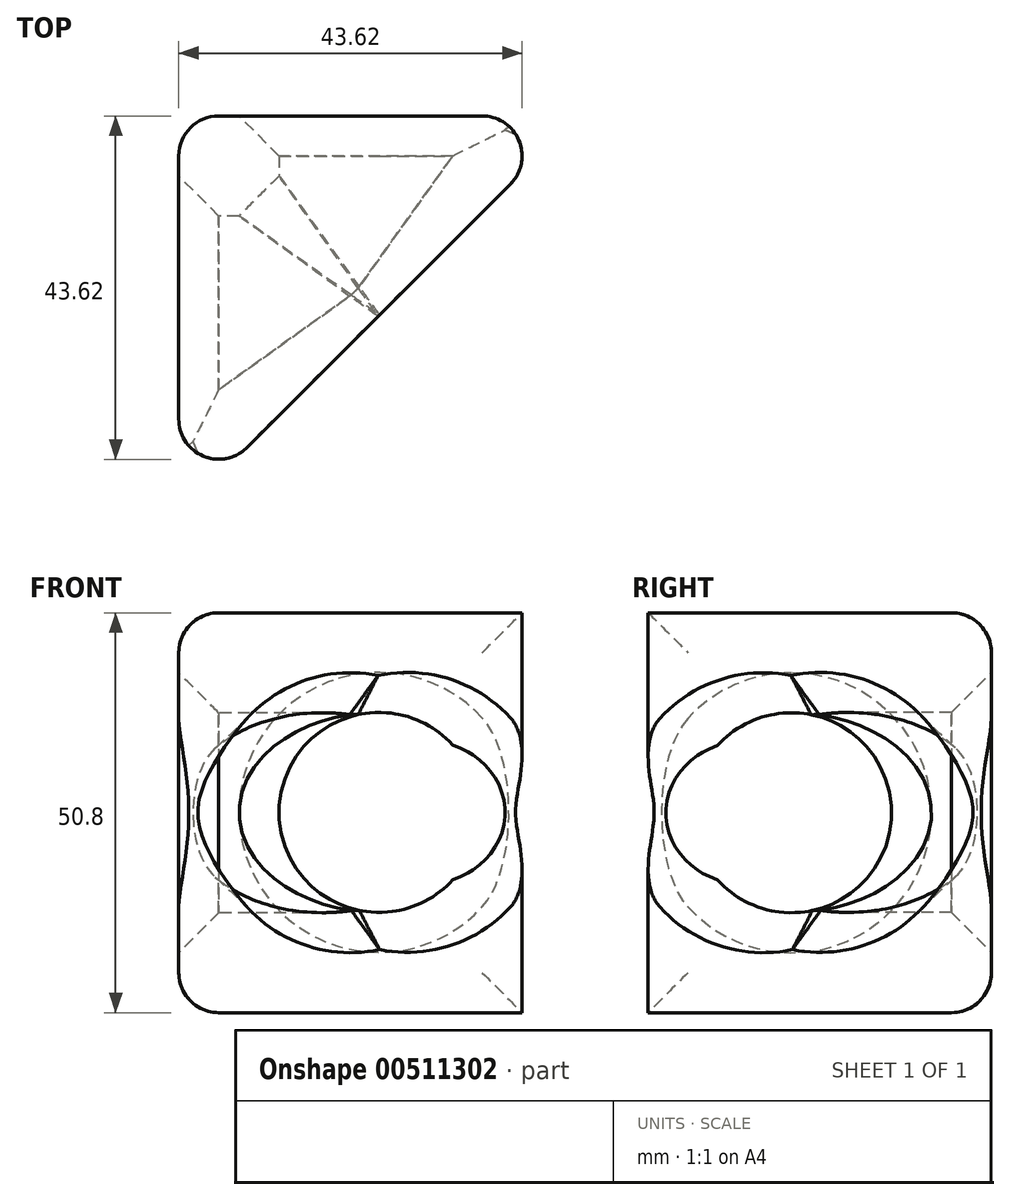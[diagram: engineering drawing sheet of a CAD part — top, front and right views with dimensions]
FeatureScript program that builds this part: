
annotation { "Feature Type Name" : "Feature", "Feature Type Description" : "" }
export const myFeature = defineFeature(function(context is Context, id is Id, definition is map)
    precondition{}
    {
        {
            var Q0;
            Q0=qCreatedBy(makeId("Front.planeOp"),FACE);
            var sketch = newSketch(context, id + "F0", { "sketchPlane" : qUnion([Q0])});
            skLineSegment(sketch, "E0", {"start": v(0, 0) * mm, "end": v(50.8, 0) * mm});
            skLineSegment(sketch, "E1", {"start": v(50.8, 0) * mm, "end": v(50.8, 50.8) * mm});
            skLineSegment(sketch, "E2", {"start": v(50.8, 50.8) * mm, "end": v(0, 50.8) * mm});
            skLineSegment(sketch, "E3", {"start": v(0, 0) * mm, "end": v(0, 50.8) * mm});
            skSolve(sketch);
        }
        {
            var Q0;
            Q0 = qSketchRegion(id + "F0", true);
            extrude(context, id + "F1", {"entities" : qUnion([Q0]), "depth" : 50.8 * mm, "offsetDistance" : 25.4 * mm});
        }
        {
            var Q0;
            Q0=makeQuery(id+"F1.opExtrude","CAP_FACE",FACE,{"disambiguationData":[OSD([sQuery(id+"F0.wireOp",EDGE,"E0"),sQuery(id+"F0.wireOp",EDGE,"E1"),sQuery(id+"F0.wireOp",EDGE,"E2"),sQuery(id+"F0.wireOp",EDGE,"E3")])],"isStart":false});
            var sketch = newSketch(context, id + "F2", { "sketchPlane" : qUnion([Q0])});
            skLineSegment(sketch, "E4", {"start": v(50.8, 50.8) * mm, "end": v(0, 0) * mm});
            skLineSegment(sketch, "E5", {"start": v(50.88, 0) * mm, "end": v(0, 50.88) * mm});
            skCircle(sketch, "E6", {"center": v(25.44, 25.44) * mm, "radius": 12.7 * mm});
            skSolve(sketch);
        }
        {
            var Q0;
            Q0 = qSketchRegion(id + "F2", true);
            extrude(context, id + "F3", {"entities" : qUnion([Q0]), "operationType" : NewBodyOperationType.REMOVE, "oppositeDirection" : true, "depth" : 50.8 * mm, "offsetDistance" : 25.4 * mm});
        }
        {
            var Q0;
            Q0=makeQuery(id+"F1.opExtrude","SWEPT_FACE",FACE,{"disambiguationData":[OSD([sQuery(id+"F0.wireOp",EDGE,"E3")])]});
            var sketch = newSketch(context, id + "F4", { "sketchPlane" : qUnion([Q0])});
            skLineSegment(sketch, "E7", {"start": v(50.8, 50.8) * mm, "end": v(0, 0) * mm});
            skLineSegment(sketch, "E8", {"start": v(50.8, 0) * mm, "end": v(0, 50.8) * mm});
            skCircle(sketch, "E9", {"center": v(25.4, 25.4) * mm, "radius": 12.7 * mm});
            skSolve(sketch);
        }
        {
            var Q0;
            Q0 = qSketchRegion(id + "F4", true);
            extrude(context, id + "F5", {"entities" : qUnion([Q0]), "operationType" : NewBodyOperationType.REMOVE, "oppositeDirection" : true, "depth" : 50.8 * mm, "offsetDistance" : 25.4 * mm});
        }
        {
            var Q0;
            Q0=makeQuery(id+"F1.opExtrude","SWEPT_FACE",FACE,{"disambiguationData":[OSD([sQuery(id+"F0.wireOp",EDGE,"E0")])]});
            var sketch = newSketch(context, id + "F6", { "sketchPlane" : qUnion([Q0])});
            skLineSegment(sketch, "E10", {"start": v(0, 0) * mm, "end": v(50.8, 50.8) * mm});
            skLineSegment(sketch, "E11", {"start": v(50.8, 50.8) * mm, "end": v(50.8, 0) * mm});
            skLineSegment(sketch, "E12", {"start": v(50.8, 0) * mm, "end": v(0, 50.8) * mm});
            skCircle(sketch, "E13", {"center": v(25.4, 25.4) * mm, "radius": 12.7 * mm});
            skSolve(sketch);
        }
        {
            var Q0;
            {var subQ0=sQuery(id+"F6.wireOp",EDGE,"E13");var subQ1=sQuery(id+"F6.wireOp",EDGE,"E10");var subQ2=makeQuery(id+"F6.imprint","INTERSECT",VERTEX,{"disambiguationData":[OD(0.0)],"derivedFrom":[subQ1,subQ0]});Q0=makeQuery(id+"F6.imprint","IMPRINT",FACE,{"disambiguationData":[TD([[makeQuery(id+"F6.imprint","IMPRINT",EDGE,{"disambiguationData":[TD([[subQ2,-1.0]])],"derivedFrom":subQ1}),-1.0]])]});}
            var Q1;
            {var subQ0=sQuery(id+"F6.wireOp",EDGE,"E13");var subQ1=sQuery(id+"F6.wireOp",EDGE,"E10");var subQ2=makeQuery(id+"F6.imprint","INTERSECT",VERTEX,{"disambiguationData":[OD(0.0)],"derivedFrom":[subQ1,subQ0]});Q1=makeQuery(id+"F6.imprint","IMPRINT",FACE,{"disambiguationData":[TD([[makeQuery(id+"F6.imprint","IMPRINT",EDGE,{"disambiguationData":[TD([[subQ2,-1.0]])],"derivedFrom":subQ1}),1.0]])]});}
            var Q2;
            {var subQ0=sQuery(id+"F6.wireOp",EDGE,"E12");var subQ1=sQuery(id+"F6.wireOp",EDGE,"E10");var subQ2=makeQuery(id+"F6.imprint","INTERSECT",VERTEX,{"derivedFrom":[subQ1,subQ0]});Q2=makeQuery(id+"F6.imprint","IMPRINT",FACE,{"disambiguationData":[TD([[makeQuery(id+"F6.imprint","IMPRINT",EDGE,{"disambiguationData":[TD([[subQ2,-1.0]])],"derivedFrom":subQ1}),-1.0]])]});}
            var Q3;
            {var subQ0=sQuery(id+"F6.wireOp",EDGE,"E12");var subQ1=sQuery(id+"F6.wireOp",EDGE,"E10");var subQ2=makeQuery(id+"F6.imprint","INTERSECT",VERTEX,{"derivedFrom":[subQ1,subQ0]});Q3=makeQuery(id+"F6.imprint","IMPRINT",FACE,{"disambiguationData":[TD([[makeQuery(id+"F6.imprint","IMPRINT",EDGE,{"disambiguationData":[TD([[subQ2,-1.0]])],"derivedFrom":subQ1}),1.0]])]});}
            extrude(context, id + "F7", {"entities" : qUnion([Q0, Q1, Q2, Q3]), "operationType" : NewBodyOperationType.REMOVE, "oppositeDirection" : true, "depth" : 50.8 * mm, "offsetDistance" : 25.4 * mm});
        }
        {
            var Q0;
            Q0=makeQuery(id+"F1.opExtrude","CAP_EDGE",EDGE,{"disambiguationData":[OSD([sQuery(id+"F0.wireOp",EDGE,"E1")])],"isStart":false});
            var Q1;
            Q1=makeQuery(id+"F1.opExtrude","CAP_EDGE",EDGE,{"disambiguationData":[OSD([sQuery(id+"F0.wireOp",EDGE,"E2")])],"isStart":false});
            var Q2;
            Q2=makeQuery(id+"F1.opExtrude","CAP_EDGE",EDGE,{"disambiguationData":[OSD([sQuery(id+"F0.wireOp",EDGE,"E0")])],"isStart":false});
            var Q3;
            Q3=makeQuery(id+"F1.opExtrude","SWEPT_EDGE",EDGE,{"disambiguationData":[OSD([sQuery(id+"F0.wireOp",EDGE,"E0"),sQuery(id+"F0.wireOp",EDGE,"E1")])]});
            var Q4;
            Q4=makeQuery(id+"F1.opExtrude","CAP_EDGE",EDGE,{"disambiguationData":[OSD([sQuery(id+"F0.wireOp",EDGE,"E1")])],"isStart":true});
            var Q5;
            Q5=makeQuery(id+"F1.opExtrude","SWEPT_EDGE",EDGE,{"disambiguationData":[OSD([sQuery(id+"F0.wireOp",EDGE,"E1"),sQuery(id+"F0.wireOp",EDGE,"E2")])]});
            var Q6;
            Q6=makeQuery(id+"F1.opExtrude","CAP_EDGE",EDGE,{"disambiguationData":[OSD([sQuery(id+"F0.wireOp",EDGE,"E2")])],"isStart":true});
            var Q7;
            Q7=makeQuery(id+"F1.opExtrude","SWEPT_EDGE",EDGE,{"disambiguationData":[OSD([sQuery(id+"F0.wireOp",EDGE,"E2"),sQuery(id+"F0.wireOp",EDGE,"E3")])]});
            var Q8;
            Q8=makeQuery(id+"F1.opExtrude","CAP_EDGE",EDGE,{"disambiguationData":[OSD([sQuery(id+"F0.wireOp",EDGE,"E3")])],"isStart":false});
            var Q9;
            Q9=makeQuery(id+"F1.opExtrude","SWEPT_EDGE",EDGE,{"disambiguationData":[OSD([sQuery(id+"F0.wireOp",EDGE,"E0"),sQuery(id+"F0.wireOp",EDGE,"E3")])]});
            var Q10;
            Q10=makeQuery(id+"F1.opExtrude","CAP_EDGE",EDGE,{"disambiguationData":[OSD([sQuery(id+"F0.wireOp",EDGE,"E0")])],"isStart":true});
            var Q11;
            Q11=makeQuery(id+"F1.opExtrude","CAP_EDGE",EDGE,{"disambiguationData":[OSD([sQuery(id+"F0.wireOp",EDGE,"E3")])],"isStart":true});
            fillet(context, id + "F8", {"entities" : qUnion([Q0, Q1, Q2, Q3, Q4, Q5, Q6, Q7, Q8, Q9, Q10, Q11]), "radius" : 5.08 * mm, "tangentPropagation" : true, "allowEdgeOverflow" : false});
        }
        {
            var Q0;
            Q0=makeQuery(id+"F7.boolean.opBoolean","SPLIT",FACE,{"disambiguationData":[TD([makeQuery(id+"F1.opExtrude","SWEPT_FACE",FACE,{"disambiguationData":[OSD([sQuery(id+"F0.wireOp",EDGE,"E3")])]})])],"derivedFrom":makeQuery(id+"F5.boolean.opBoolean","COPY",FACE,{"derivedFrom":makeQuery(id+"F5.opExtrude","SWEPT_FACE",FACE,{"disambiguationData":[OSD([sQuery(id+"F4.wireOp",EDGE,"E9")])]})})});
            var Q1;
            Q1=makeQuery(id+"F7.boolean.opBoolean","SPLIT",FACE,{"disambiguationData":[TD([makeQuery(id+"F1.opExtrude","CAP_FACE",FACE,{"disambiguationData":[OSD([sQuery(id+"F0.wireOp",EDGE,"E0"),sQuery(id+"F0.wireOp",EDGE,"E1"),sQuery(id+"F0.wireOp",EDGE,"E2"),sQuery(id+"F0.wireOp",EDGE,"E3")])],"isStart":false})])],"derivedFrom":makeQuery(id+"F3.boolean.opBoolean","COPY",FACE,{"derivedFrom":makeQuery(id+"F3.opExtrude","SWEPT_FACE",FACE,{"disambiguationData":[OSD([sQuery(id+"F2.wireOp",EDGE,"E6")])]})})});
            var Q2;
            Q2=makeQuery(id+"F7.boolean.opBoolean","SPLIT",FACE,{"disambiguationData":[TD([makeQuery(id+"F1.opExtrude","SWEPT_FACE",FACE,{"disambiguationData":[OSD([sQuery(id+"F0.wireOp",EDGE,"E1")])]})])],"derivedFrom":makeQuery(id+"F5.boolean.opBoolean","COPY",FACE,{"derivedFrom":makeQuery(id+"F5.opExtrude","SWEPT_FACE",FACE,{"disambiguationData":[OSD([sQuery(id+"F4.wireOp",EDGE,"E9")])]})})});
            var Q3;
            Q3=makeQuery(id+"F3.boolean.opBoolean","COPY",EDGE,{"derivedFrom":makeQuery(id+"F3.opExtrude","CAP_EDGE",EDGE,{"disambiguationData":[OSD([sQuery(id+"F2.wireOp",EDGE,"E6")])],"isStart":false})});
            var Q4;
            Q4=makeQuery(id+"F7.boolean.opBoolean","COPY",EDGE,{"derivedFrom":makeQuery(id+"F7.opExtrude","CAP_EDGE",EDGE,{"disambiguationData":[OSD([sQuery(id+"F6.wireOp",EDGE,"E13")])],"isStart":true})});
            var Q5;
            Q5=makeQuery(id+"F7.boolean.opBoolean","COPY",EDGE,{"derivedFrom":makeQuery(id+"F7.opExtrude","CAP_EDGE",EDGE,{"disambiguationData":[OSD([sQuery(id+"F6.wireOp",EDGE,"E13")])],"isStart":false})});
            chamfer(context, id + "F9", {"entities" : qUnion([Q0, Q1, Q2, Q3, Q4, Q5]), "width" : 5.08 * mm, "tangentPropagation" : true});
        }
    });
